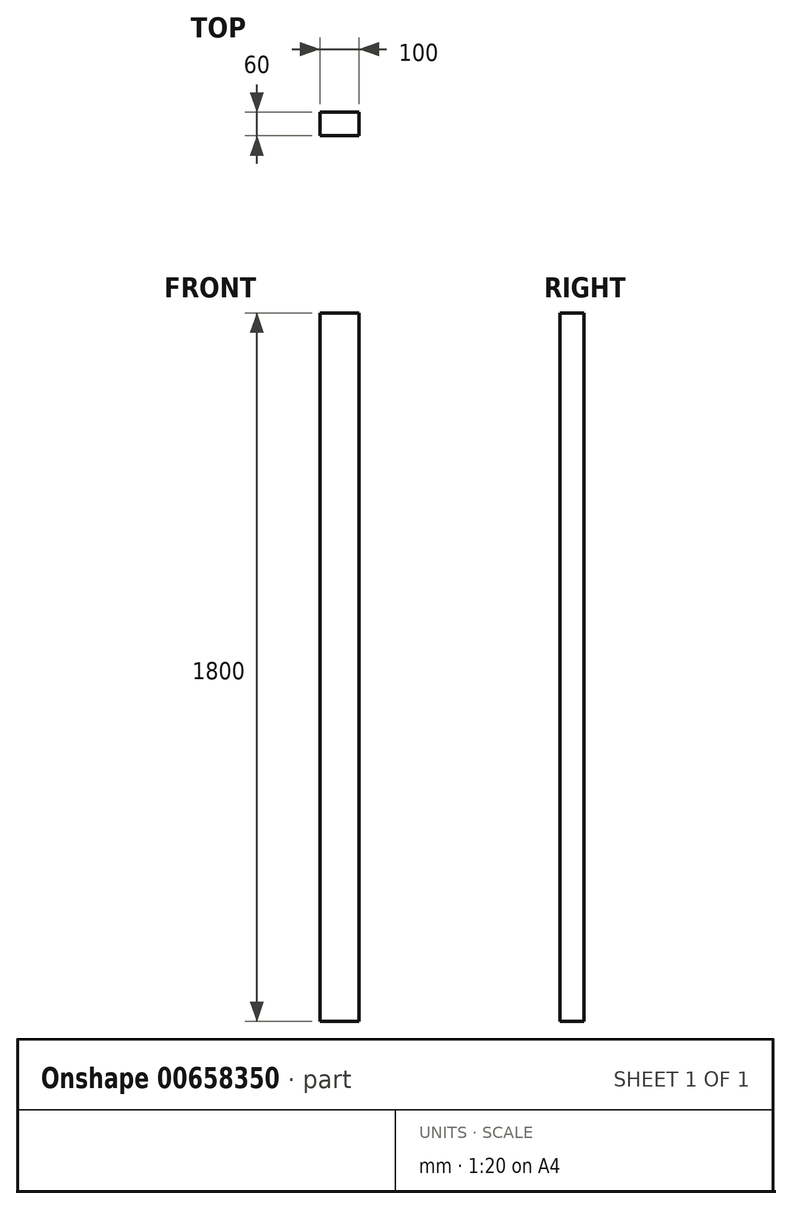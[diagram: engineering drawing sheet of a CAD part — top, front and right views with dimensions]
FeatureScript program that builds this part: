
annotation { "Feature Type Name" : "Feature", "Feature Type Description" : "" }
export const myFeature = defineFeature(function(context is Context, id is Id, definition is map)
    precondition{}
    {
        {
            var Q0;
            Q0=qCreatedBy(makeId("Top.planeOp"),FACE);
            var sketch = newSketch(context, id + "F0", { "sketchPlane" : qUnion([Q0])});
            skLineSegment(sketch, "E0.bottom", {"start": v(-45, 4.68) * mm, "end": v(55, 4.68) * mm});
            skLineSegment(sketch, "E0.top", {"start": v(-45, -55.32) * mm, "end": v(55, -55.32) * mm});
            skLineSegment(sketch, "E0.left", {"start": v(-45, 4.68) * mm, "end": v(-45, -55.32) * mm});
            skLineSegment(sketch, "E0.right", {"start": v(55, 4.68) * mm, "end": v(55, -55.32) * mm});
            skSolve(sketch);
        }
        {
            var Q0;
            Q0=qSketchRegion(id+"F0",true);
            extrude(context, id + "F1", {"entities" : qUnion([Q0]), "depth" : 1800 * mm, "offsetDistance" : 25 * mm});
        }
    });
